# Revit family: Thorn XETARO
name_source: partatom
category: Lighting Fixtures
revit_build: Autodesk Revit 2018 (Build: 20170223_1515(x64)
units: mm (PartAtom-declared; Revit-internal decimal feet)

## family parameters
Cut with Voids When Loaded = No
Host = Face
Light Source = Yes
OmniClass Number = 23.80.70.11
OmniClass Title = Luminaries for Internal Lighting
Part Type = Normal
Room Calculation Point = No
Round Connector Dimension = Use Diameter
Shared = No

## types (2) — shared parameters
Assembly Code = D5020210
Body = ZG_PMMA_Grey
Color Filter = 16777215
Cover = ZG_PMMA_Semitransparent_SI
Description = Moisture-proof diffuser luminaire
Dimming Lamp Color Temperature Shift = <None>
Emit Shape Visible in Rendering = No
Emit from Rectangle Length = 145 mm  [stored 0.475722 ft]
Height = 100 mm  [stored 0.328084 ft]
Lamp = LED
Manufacturer = Thorn Lighting
Tilt Angle = -90.00°
URL = http://thornlighting.com
Voltage = 230 V
Width = 145 mm  [stored 0.475722 ft]
zero-valued in all types: Default Elevation

## per-type parameters (varying)
| type | Apparent Load | Emit from Rectangle Width | Fixing Length | Length | Model | Photometric Web File |
| XETARO M | 31 VA | 1272 mm  [stored 4.17323 ft] | 700 mm  [stored 2.29659 ft] | 1272 mm  [stored 4.17323 ft] | 96701888 | 96701888_(STD).IES |
| XETARO L | 38 VA | 1572 mm  [stored 5.15748 ft] | 950 mm  [stored 3.1168 ft] | 1572 mm  [stored 5.15748 ft] | 96701889 | 96701889_(STD).IES |

note: [stored X ft] marks values corroborated as IEEE doubles in the binary element streams (Revit-internal decimal feet)

## geometry (parser evidence)
native form markers: Blend x2, Sweep x2
no freeform markers — native parametric forms only
